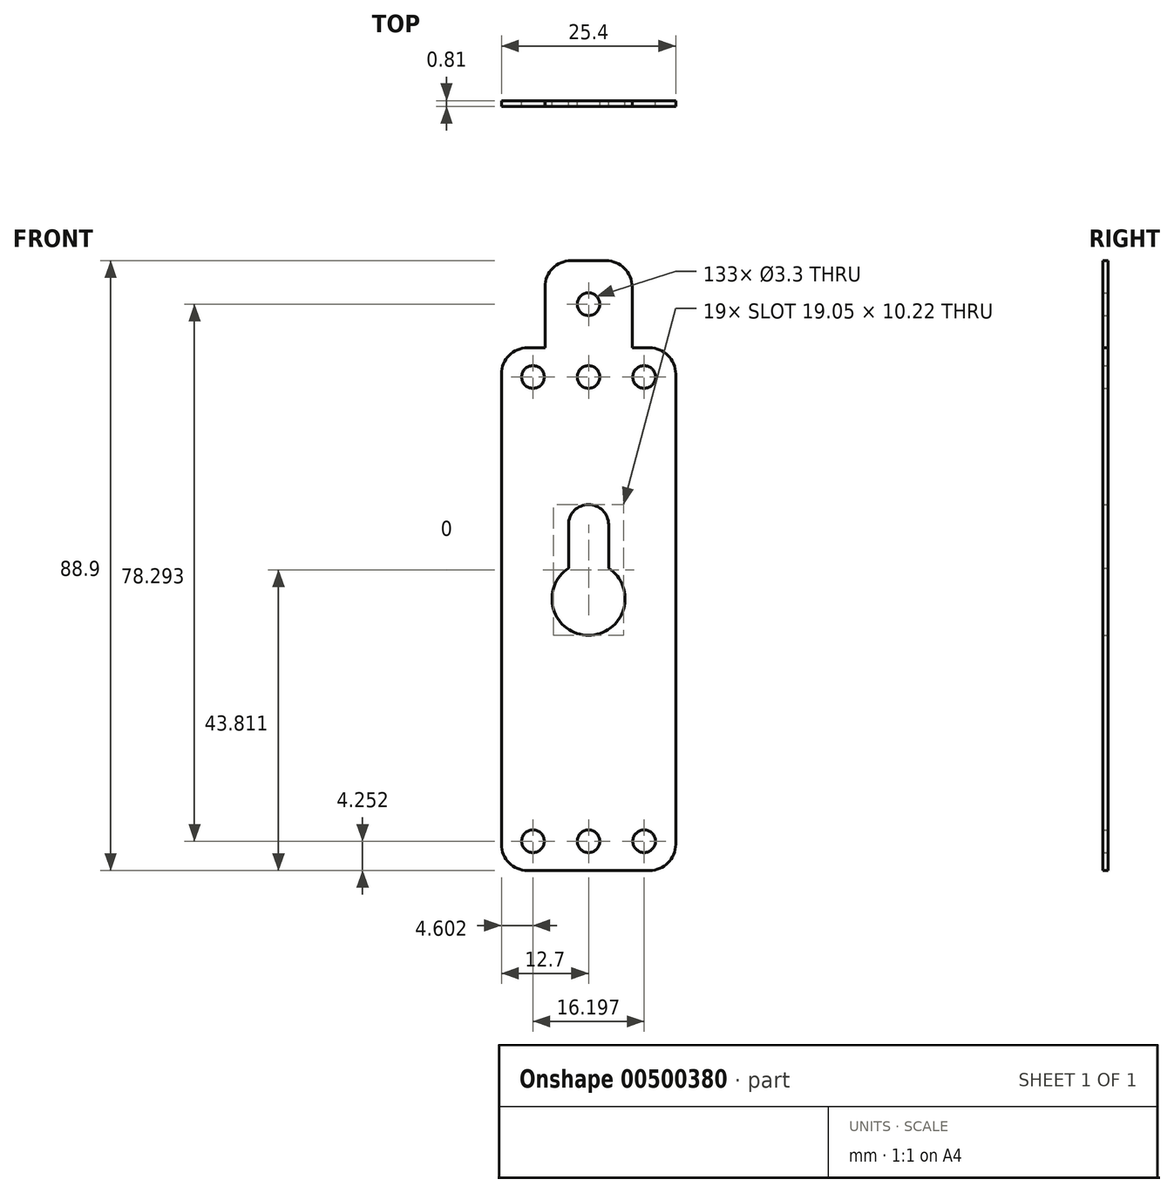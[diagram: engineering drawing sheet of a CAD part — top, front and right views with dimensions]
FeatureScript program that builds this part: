
annotation { "Feature Type Name" : "Feature", "Feature Type Description" : "" }
export const myFeature = defineFeature(function(context is Context, id is Id, definition is map)
    precondition{}
    {
        {
            var Q0;
            Q0=qCreatedBy(makeId("Front.planeOp"),FACE);
            var sketch = newSketch(context, id + "F0", { "sketchPlane" : qUnion([Q0])});
            skArc(sketch, "E0", {"start": v(-2.92, 4.46) * mm, "mid": v(0, -5.33) * mm, "end": v(2.92, 4.46) * mm});
            skLineSegment(sketch, "E1.left", {"start": v(2.92, 10.8) * mm, "end": v(2.92, 4.46) * mm});
            skLineSegment(sketch, "E1.right", {"start": v(-2.92, 10.8) * mm, "end": v(-2.92, 4.46) * mm});
            skArc(sketch, "E2", {"start": v(2.92, 10.8) * mm, "mid": v(0, 13.72) * mm, "end": v(-2.92, 10.8) * mm});
            skLineSegment(sketch, "E3.bottom", {"start": v(-8.9, 36.58) * mm, "end": v(8.89, 36.58) * mm});
            skLineSegment(sketch, "E3.top", {"start": v(-8.9, -39.62) * mm, "end": v(8.89, -39.62) * mm});
            skLineSegment(sketch, "E3.left", {"start": v(-12.7, 32.77) * mm, "end": v(-12.7, -35.81) * mm});
            skLineSegment(sketch, "E3.right", {"start": v(12.7, 32.77) * mm, "end": v(12.7, -35.81) * mm});
            skCircle(sketch, "E4", {"center": v(0, 32.32) * mm, "radius": 1.65 * mm});
            skCircle(sketch, "E5", {"center": v(-8.1, 32.32) * mm, "radius": 1.65 * mm});
            skCircle(sketch, "E6.MirrorC", {"center": v(8.1, 32.32) * mm, "radius": 1.65 * mm});
            skLineSegment(sketch, "E7", {"start": v(-12.7, -1.52) * mm, "end": v(12.7, -1.52) * mm, "construction": true});
            skCircle(sketch, "E8.MirrorC", {"center": v(8.1, -35.37) * mm, "radius": 1.65 * mm});
            skCircle(sketch, "E9.MirrorC", {"center": v(0, -35.37) * mm, "radius": 1.65 * mm});
            skCircle(sketch, "E10.MirrorC", {"center": v(-8.1, -35.37) * mm, "radius": 1.65 * mm});
            skPoint(sketch, "E11.visualSharp", {"position": v(-12.7, 36.58) * mm});
            skArc(sketch, "E11.filletArc", {"start": v(-8.9, 36.58) * mm, "mid": v(-11.58, 35.46) * mm, "end": v(-12.7, 32.77) * mm});
            skPoint(sketch, "E12.visualSharp", {"position": v(12.7, 36.58) * mm});
            skArc(sketch, "E12.filletArc", {"start": v(12.7, 32.77) * mm, "mid": v(11.58, 35.46) * mm, "end": v(8.89, 36.58) * mm});
            skPoint(sketch, "E13.visualSharp", {"position": v(12.7, -39.62) * mm});
            skArc(sketch, "E13.filletArc", {"start": v(8.89, -39.62) * mm, "mid": v(11.58, -38.5) * mm, "end": v(12.7, -35.81) * mm});
            skPoint(sketch, "E14.visualSharp", {"position": v(-12.7, -39.62) * mm});
            skArc(sketch, "E14.filletArc", {"start": v(-12.7, -35.81) * mm, "mid": v(-11.58, -38.5) * mm, "end": v(-8.9, -39.62) * mm});
            skLineSegment(sketch, "E15", {"start": v(0, 36.58) * mm, "end": v(0, -39.62) * mm, "construction": true});
            skPoint(sketch, "E16", {"position": v(0, -1.52) * mm});
            skLineSegment(sketch, "E17.bottom", {"start": v(-2.54, 49.28) * mm, "end": v(2.54, 49.28) * mm});
            skLineSegment(sketch, "E17.left", {"start": v(-6.35, 45.47) * mm, "end": v(-6.35, 36.58) * mm});
            skLineSegment(sketch, "E17.right", {"start": v(6.35, 45.47) * mm, "end": v(6.35, 36.58) * mm});
            skPoint(sketch, "E17.middle", {"position": v(0, 36.58) * mm});
            skPoint(sketch, "E18.orphan", {"position": v(6.35, 23.88) * mm});
            skPoint(sketch, "E19.orphan", {"position": v(-6.35, 23.88) * mm});
            skCircle(sketch, "E20", {"center": v(0, 42.93) * mm, "radius": 1.65 * mm});
            skPoint(sketch, "E21.visualSharp", {"position": v(-6.35, 49.28) * mm});
            skArc(sketch, "E21.filletArc", {"start": v(-2.54, 49.28) * mm, "mid": v(-5.23, 48.16) * mm, "end": v(-6.35, 45.47) * mm});
            skPoint(sketch, "E22.visualSharp", {"position": v(6.35, 49.28) * mm});
            skArc(sketch, "E22.filletArc", {"start": v(6.35, 45.47) * mm, "mid": v(5.23, 48.16) * mm, "end": v(2.54, 49.28) * mm});
            skLineSegment(sketch, "E23", {"start": v(-6.35, 36.58) * mm, "end": v(6.35, 49.28) * mm, "construction": true});
            skSolve(sketch);
        }
        {
            var Q0;
            Q0 = qSketchRegion(id + "F0", true);
            extrude(context, id + "F1", {"entities" : qUnion([Q0]), "depth" : 0.81 * mm});
        }
    });
